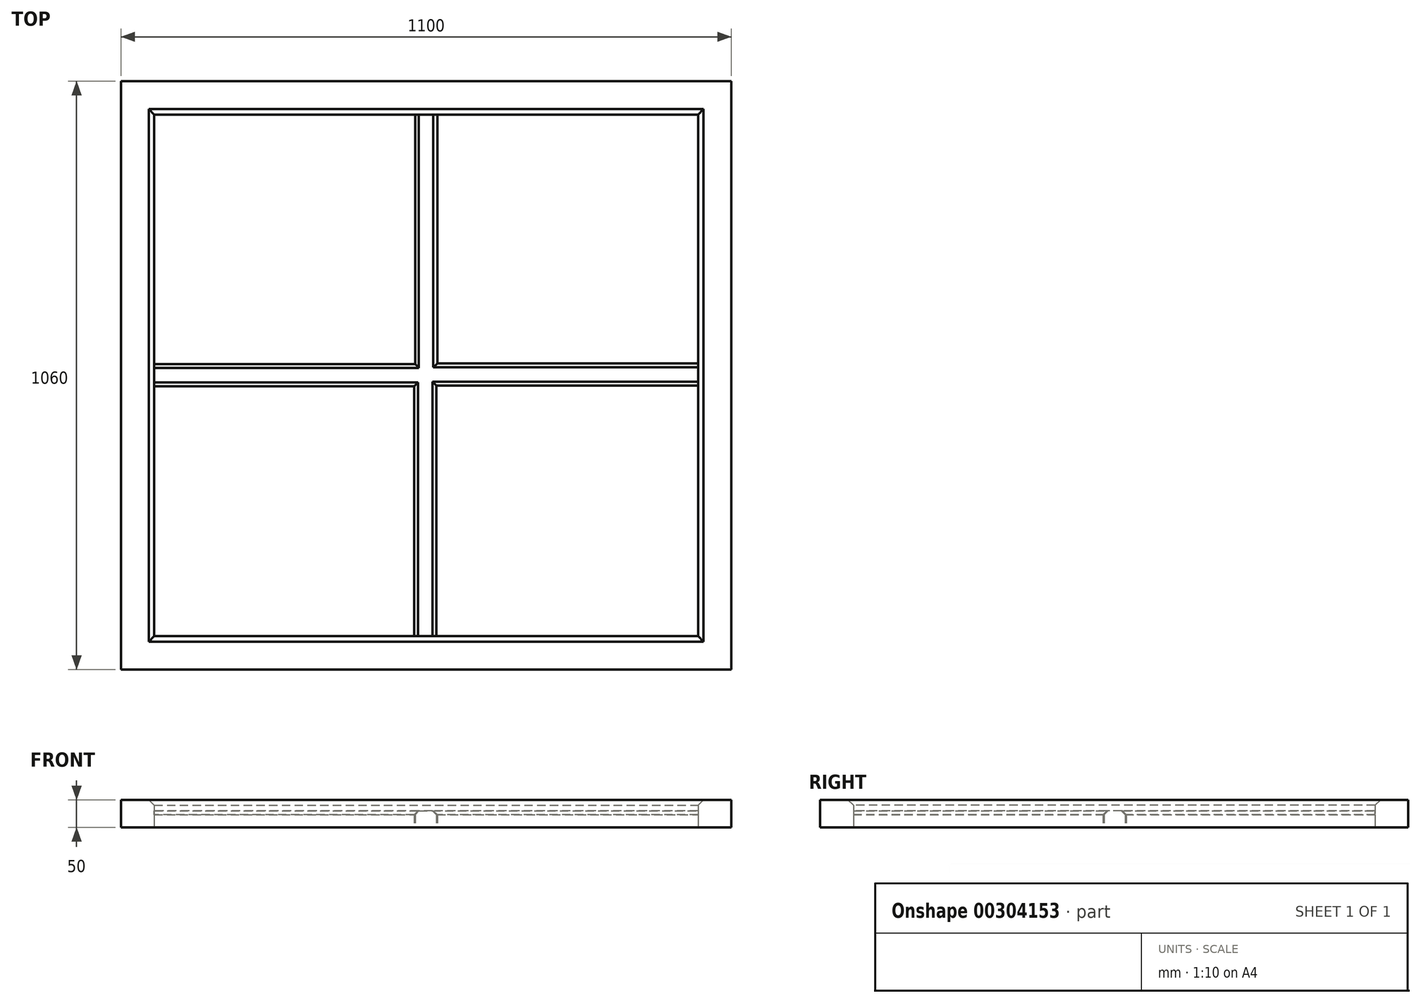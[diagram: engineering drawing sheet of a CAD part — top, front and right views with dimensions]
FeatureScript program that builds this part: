
annotation { "Feature Type Name" : "Feature", "Feature Type Description" : "" }
export const myFeature = defineFeature(function(context is Context, id is Id, definition is map)
    precondition{}
    {
        {
            var Q0;
            Q0=qCreatedBy(makeId("Top.planeOp"),FACE);
            var sketch = newSketch(context, id + "F0", { "sketchPlane" : qUnion([Q0])});
            skLineSegment(sketch, "E0.bottom", {"start": v(-377.87, 523.39) * mm, "end": v(722.13, 523.39) * mm});
            skLineSegment(sketch, "E0.top", {"start": v(-377.87, -536.61) * mm, "end": v(722.13, -536.61) * mm});
            skLineSegment(sketch, "E0.left", {"start": v(-377.87, 523.39) * mm, "end": v(-377.87, -536.61) * mm});
            skLineSegment(sketch, "E0.right", {"start": v(722.13, 523.39) * mm, "end": v(722.13, -536.61) * mm});
            skLineSegment(sketch, "E1.bottom", {"start": v(-317.87, 463.39) * mm, "end": v(152.13, 463.39) * mm});
            skLineSegment(sketch, "E1.top", {"start": v(-317.87, 13.39) * mm, "end": v(152.13, 13.39) * mm});
            skLineSegment(sketch, "E1.left", {"start": v(-317.87, 463.39) * mm, "end": v(-317.87, 13.39) * mm});
            skLineSegment(sketch, "E1.right", {"start": v(152.13, 463.39) * mm, "end": v(152.13, 13.39) * mm});
            skLineSegment(sketch, "E2.bottom", {"start": v(192.13, 463.39) * mm, "end": v(662.13, 463.39) * mm});
            skLineSegment(sketch, "E2.top", {"start": v(192.13, 15.2) * mm, "end": v(662.13, 15.2) * mm});
            skLineSegment(sketch, "E2.left", {"start": v(192.13, 463.39) * mm, "end": v(192.13, 15.2) * mm});
            skLineSegment(sketch, "E2.right", {"start": v(662.13, 463.39) * mm, "end": v(662.13, 15.2) * mm});
            skLineSegment(sketch, "E3.bottom", {"start": v(-317.87, -26.61) * mm, "end": v(150.31, -26.61) * mm});
            skLineSegment(sketch, "E3.top", {"start": v(-317.87, -476.61) * mm, "end": v(150.31, -476.61) * mm});
            skLineSegment(sketch, "E3.left", {"start": v(-317.87, -26.61) * mm, "end": v(-317.87, -476.61) * mm});
            skLineSegment(sketch, "E3.right", {"start": v(150.31, -26.61) * mm, "end": v(150.31, -476.61) * mm});
            skLineSegment(sketch, "E4.bottom", {"start": v(190.31, -24.8) * mm, "end": v(662.13, -24.8) * mm});
            skLineSegment(sketch, "E4.top", {"start": v(190.31, -476.61) * mm, "end": v(662.13, -476.61) * mm});
            skLineSegment(sketch, "E4.left", {"start": v(190.31, -24.8) * mm, "end": v(190.31, -476.61) * mm});
            skLineSegment(sketch, "E4.right", {"start": v(662.13, -24.8) * mm, "end": v(662.13, -476.61) * mm});
            skLineSegment(sketch, "E5", {"start": v(-317.87, 13.39) * mm, "end": v(-317.87, -26.61) * mm});
            skLineSegment(sketch, "E6", {"start": v(152.13, 463.39) * mm, "end": v(192.13, 463.39) * mm});
            skLineSegment(sketch, "E7", {"start": v(662.13, 15.2) * mm, "end": v(662.13, -24.8) * mm});
            skLineSegment(sketch, "E8", {"start": v(190.31, -476.61) * mm, "end": v(150.31, -476.61) * mm});
            skSolve(sketch);
        }
        {
            var Q0;
            Q0=makeQuery(id+"F0.imprint","IMPRINT",FACE,{"disambiguationData":[TD([[makeQuery(id+"F0.imprint","IMPRINT",EDGE,{"derivedFrom":sQuery(id+"F0.wireOp",EDGE,"E0.bottom")}),-1.0]])]});
            extrude(context, id + "F1", {"entities" : qUnion([Q0]), "depth" : 50 * mm, "offsetDistance" : 25 * mm});
        }
        {
            var Q0;
            Q0=makeQuery(id+"F1.opExtrude","CAP_EDGE",EDGE,{"disambiguationData":[OSD([sQuery(id+"F0.wireOp",EDGE,"ytPpMPqZ-kEHr-QmaY-d1DR-AzYH62YFSOlj.left")])],"isStart":false});
            var Q1;
            Q1=makeQuery(id+"F1.opExtrude","CAP_EDGE",EDGE,{"disambiguationData":[OSD([sQuery(id+"F0.wireOp",EDGE,"ytPpMPqZ-kEHr-QmaY-d1DR-AzYH62YFSOlj.bottom")])],"isStart":false});
            var Q2;
            Q2=makeQuery(id+"F1.opExtrude","CAP_EDGE",EDGE,{"disambiguationData":[OSD([sQuery(id+"F0.wireOp",EDGE,"ytPpMPqZ-kEHr-QmaY-d1DR-AzYH62YFSOlj.right")])],"isStart":false});
            var Q3;
            Q3=makeQuery(id+"F1.opExtrude","CAP_EDGE",EDGE,{"disambiguationData":[OSD([sQuery(id+"F0.wireOp",EDGE,"ytPpMPqZ-kEHr-QmaY-d1DR-AzYH62YFSOlj.top")])],"isStart":false});
            var Q4;
            Q4=makeQuery(id+"F1.opExtrude","CAP_EDGE",EDGE,{"disambiguationData":[OSD([sQuery(id+"F0.wireOp",EDGE,"r7QiBjje-UKbf-qYST-CBBd-TYCSkPhiPhca.top")])],"isStart":false});
            var Q5;
            Q5=makeQuery(id+"F1.opExtrude","CAP_EDGE",EDGE,{"disambiguationData":[OSD([sQuery(id+"F0.wireOp",EDGE,"r7QiBjje-UKbf-qYST-CBBd-TYCSkPhiPhca.bottom")])],"isStart":false});
            var Q6;
            Q6=makeQuery(id+"F1.opExtrude","CAP_EDGE",EDGE,{"disambiguationData":[OSD([sQuery(id+"F0.wireOp",EDGE,"r7QiBjje-UKbf-qYST-CBBd-TYCSkPhiPhca.left")])],"isStart":false});
            var Q7;
            Q7=makeQuery(id+"F1.opExtrude","CAP_EDGE",EDGE,{"disambiguationData":[OSD([sQuery(id+"F0.wireOp",EDGE,"r7QiBjje-UKbf-qYST-CBBd-TYCSkPhiPhca.right")])],"isStart":false});
            var Q8;
            Q8=makeQuery(id+"F1.opExtrude","CAP_EDGE",EDGE,{"disambiguationData":[OSD([sQuery(id+"F0.wireOp",EDGE,"HfWFaPNu-mQyP-ler6-jSu7-HC3u6uNNGoQA.left")])],"isStart":false});
            var Q9;
            Q9=makeQuery(id+"F1.opExtrude","CAP_EDGE",EDGE,{"disambiguationData":[OSD([sQuery(id+"F0.wireOp",EDGE,"HfWFaPNu-mQyP-ler6-jSu7-HC3u6uNNGoQA.bottom")])],"isStart":false});
            var Q10;
            Q10=makeQuery(id+"F1.opExtrude","CAP_EDGE",EDGE,{"disambiguationData":[OSD([sQuery(id+"F0.wireOp",EDGE,"HfWFaPNu-mQyP-ler6-jSu7-HC3u6uNNGoQA.right")])],"isStart":false});
            var Q11;
            Q11=makeQuery(id+"F1.opExtrude","CAP_EDGE",EDGE,{"disambiguationData":[OSD([sQuery(id+"F0.wireOp",EDGE,"HfWFaPNu-mQyP-ler6-jSu7-HC3u6uNNGoQA.top")])],"isStart":false});
            var Q12;
            Q12=makeQuery(id+"F1.opExtrude","CAP_EDGE",EDGE,{"disambiguationData":[OSD([sQuery(id+"F0.wireOp",EDGE,"5wbdZzbv-KT36-aS9W-tHdP-7188U3jB6Ytn.bottom")])],"isStart":false});
            var Q13;
            Q13=makeQuery(id+"F1.opExtrude","CAP_EDGE",EDGE,{"disambiguationData":[OSD([sQuery(id+"F0.wireOp",EDGE,"5wbdZzbv-KT36-aS9W-tHdP-7188U3jB6Ytn.left")])],"isStart":false});
            var Q14;
            Q14=makeQuery(id+"F1.opExtrude","CAP_EDGE",EDGE,{"disambiguationData":[OSD([sQuery(id+"F0.wireOp",EDGE,"5wbdZzbv-KT36-aS9W-tHdP-7188U3jB6Ytn.top")])],"isStart":false});
            var Q15;
            Q15=makeQuery(id+"F1.opExtrude","CAP_EDGE",EDGE,{"disambiguationData":[OSD([sQuery(id+"F0.wireOp",EDGE,"5wbdZzbv-KT36-aS9W-tHdP-7188U3jB6Ytn.right")])],"isStart":false});
            var Q16;
            Q16=makeQuery(id+"F1.opExtrude","CAP_EDGE",EDGE,{"disambiguationData":[OSD([sQuery(id+"F0.wireOp",EDGE,"DTlHMEbU-aPmp-yZgJ-OWsR-Co97d6l2honQ.bottom")])],"isStart":false});
            var Q17;
            Q17=makeQuery(id+"F1.opExtrude","CAP_EDGE",EDGE,{"disambiguationData":[OSD([sQuery(id+"F0.wireOp",EDGE,"DTlHMEbU-aPmp-yZgJ-OWsR-Co97d6l2honQ.right")])],"isStart":false});
            var Q18;
            Q18=makeQuery(id+"F1.opExtrude","CAP_EDGE",EDGE,{"disambiguationData":[OSD([sQuery(id+"F0.wireOp",EDGE,"DTlHMEbU-aPmp-yZgJ-OWsR-Co97d6l2honQ.top")])],"isStart":false});
            var Q19;
            Q19=makeQuery(id+"F1.opExtrude","CAP_EDGE",EDGE,{"disambiguationData":[OSD([sQuery(id+"F0.wireOp",EDGE,"DTlHMEbU-aPmp-yZgJ-OWsR-Co97d6l2honQ.left")])],"isStart":false});
            var Q20;
            Q20=makeQuery(id+"F1.opExtrude","CAP_EDGE",EDGE,{"disambiguationData":[OSD([sQuery(id+"F0.wireOp",EDGE,"KnIwFXTZ-7AYv-IQ4P-MqQU-q16PSDZZjzCm.right")])],"isStart":false});
            var Q21;
            Q21=makeQuery(id+"F1.opExtrude","CAP_EDGE",EDGE,{"disambiguationData":[OSD([sQuery(id+"F0.wireOp",EDGE,"KnIwFXTZ-7AYv-IQ4P-MqQU-q16PSDZZjzCm.bottom")])],"isStart":false});
            var Q22;
            Q22=makeQuery(id+"F1.opExtrude","CAP_EDGE",EDGE,{"disambiguationData":[OSD([sQuery(id+"F0.wireOp",EDGE,"KnIwFXTZ-7AYv-IQ4P-MqQU-q16PSDZZjzCm.left")])],"isStart":false});
            var Q23;
            Q23=makeQuery(id+"F1.opExtrude","CAP_EDGE",EDGE,{"disambiguationData":[OSD([sQuery(id+"F0.wireOp",EDGE,"KnIwFXTZ-7AYv-IQ4P-MqQU-q16PSDZZjzCm.top")])],"isStart":false});
            var Q24;
            Q24=makeQuery(id+"F1.opExtrude","CAP_EDGE",EDGE,{"disambiguationData":[OSD([sQuery(id+"F0.wireOp",EDGE,"E1.left")])],"isStart":false});
            var Q25;
            Q25=makeQuery(id+"F1.opExtrude","CAP_EDGE",EDGE,{"disambiguationData":[OSD([sQuery(id+"F0.wireOp",EDGE,"E1.bottom")])],"isStart":false});
            var Q26;
            Q26=makeQuery(id+"F1.opExtrude","CAP_EDGE",EDGE,{"disambiguationData":[OSD([sQuery(id+"F0.wireOp",EDGE,"E1.right")])],"isStart":false});
            var Q27;
            Q27=makeQuery(id+"F1.opExtrude","CAP_EDGE",EDGE,{"disambiguationData":[OSD([sQuery(id+"F0.wireOp",EDGE,"E2.left")])],"isStart":false});
            var Q28;
            Q28=makeQuery(id+"F1.opExtrude","CAP_EDGE",EDGE,{"disambiguationData":[OSD([sQuery(id+"F0.wireOp",EDGE,"E3.bottom")])],"isStart":false});
            var Q29;
            Q29=makeQuery(id+"F1.opExtrude","CAP_EDGE",EDGE,{"disambiguationData":[OSD([sQuery(id+"F0.wireOp",EDGE,"E4.bottom")])],"isStart":false});
            var Q30;
            Q30=makeQuery(id+"F1.opExtrude","CAP_EDGE",EDGE,{"disambiguationData":[OSD([sQuery(id+"F0.wireOp",EDGE,"E4.left")])],"isStart":false});
            var Q31;
            Q31=makeQuery(id+"F1.opExtrude","CAP_EDGE",EDGE,{"disambiguationData":[OSD([sQuery(id+"F0.wireOp",EDGE,"E2.bottom")])],"isStart":false});
            var Q32;
            Q32=makeQuery(id+"F1.opExtrude","CAP_EDGE",EDGE,{"disambiguationData":[OSD([sQuery(id+"F0.wireOp",EDGE,"E3.left")])],"isStart":false});
            var Q33;
            Q33=makeQuery(id+"F1.opExtrude","CAP_EDGE",EDGE,{"disambiguationData":[OSD([sQuery(id+"F0.wireOp",EDGE,"E2.right")])],"isStart":false});
            var Q34;
            Q34=makeQuery(id+"F1.opExtrude","CAP_EDGE",EDGE,{"disambiguationData":[OSD([sQuery(id+"F0.wireOp",EDGE,"E4.right")])],"isStart":false});
            var Q35;
            Q35=makeQuery(id+"F1.opExtrude","CAP_EDGE",EDGE,{"disambiguationData":[OSD([sQuery(id+"F0.wireOp",EDGE,"E4.top")])],"isStart":false});
            var Q36;
            Q36=makeQuery(id+"F1.opExtrude","CAP_EDGE",EDGE,{"disambiguationData":[OSD([sQuery(id+"F0.wireOp",EDGE,"E3.top")])],"isStart":false});
            var Q37;
            Q37=makeQuery(id+"F1.opExtrude","CAP_EDGE",EDGE,{"disambiguationData":[OSD([sQuery(id+"F0.wireOp",EDGE,"E3.right")])],"isStart":false});
            var Q38;
            Q38=makeQuery(id+"F1.opExtrude","CAP_EDGE",EDGE,{"disambiguationData":[OSD([sQuery(id+"F0.wireOp",EDGE,"E2.top")])],"isStart":false});
            var Q39;
            Q39=makeQuery(id+"F1.opExtrude","CAP_EDGE",EDGE,{"disambiguationData":[OSD([sQuery(id+"F0.wireOp",EDGE,"E1.top")])],"isStart":false});
            chamfer(context, id + "F2", {"entities" : qUnion([Q0, Q1, Q2, Q3, Q4, Q5, Q6, Q7, Q8, Q9, Q10, Q11, Q12, Q13, Q14, Q15, Q16, Q17, Q18, Q19, Q20, Q21, Q22, Q23, Q24, Q25, Q26, Q27, Q28, Q29, Q30, Q31, Q32, Q33, Q34, Q35, Q36, Q37, Q38, Q39]), "width" : 10 * mm, "tangentPropagation" : true});
        }
        {
            var Q0;
            Q0=makeQuery(id+"F0.imprint","IMPRINT",FACE,{"disambiguationData":[TD([[makeQuery(id+"F0.imprint","IMPRINT",EDGE,{"derivedFrom":sQuery(id+"F0.wireOp",EDGE,"E1.top")}),-1.0]])]});
            extrude(context, id + "F3", {"entities" : qUnion([Q0]), "depth" : 30 * mm, "offsetDistance" : 25 * mm});
        }
        {
            var Q0;
            Q0=makeQuery(id+"F3.opExtrude","CAP_EDGE",EDGE,{"disambiguationData":[OSD([sQuery(id+"F0.wireOp",EDGE,"E3.bottom")])],"isStart":false});
            var Q1;
            Q1=makeQuery(id+"F3.opExtrude","CAP_EDGE",EDGE,{"disambiguationData":[OSD([sQuery(id+"F0.wireOp",EDGE,"E1.top")])],"isStart":false});
            var Q2;
            Q2=makeQuery(id+"F3.opExtrude","CAP_EDGE",EDGE,{"disambiguationData":[OSD([sQuery(id+"F0.wireOp",EDGE,"E1.right")])],"isStart":false});
            var Q3;
            Q3=makeQuery(id+"F3.opExtrude","CAP_EDGE",EDGE,{"disambiguationData":[OSD([sQuery(id+"F0.wireOp",EDGE,"E2.left")])],"isStart":false});
            var Q4;
            Q4=makeQuery(id+"F3.opExtrude","CAP_EDGE",EDGE,{"disambiguationData":[OSD([sQuery(id+"F0.wireOp",EDGE,"E4.bottom")])],"isStart":false});
            var Q5;
            Q5=makeQuery(id+"F3.opExtrude","CAP_EDGE",EDGE,{"disambiguationData":[OSD([sQuery(id+"F0.wireOp",EDGE,"E2.top")])],"isStart":false});
            var Q6;
            Q6=makeQuery(id+"F3.opExtrude","CAP_EDGE",EDGE,{"disambiguationData":[OSD([sQuery(id+"F0.wireOp",EDGE,"E4.left")])],"isStart":false});
            var Q7;
            Q7=makeQuery(id+"F3.opExtrude","CAP_EDGE",EDGE,{"disambiguationData":[OSD([sQuery(id+"F0.wireOp",EDGE,"E3.right")])],"isStart":false});
            chamfer(context, id + "F4", {"entities" : qUnion([Q0, Q1, Q2, Q3, Q4, Q5, Q6, Q7]), "width" : 7 * mm, "tangentPropagation" : true});
        }
    });
